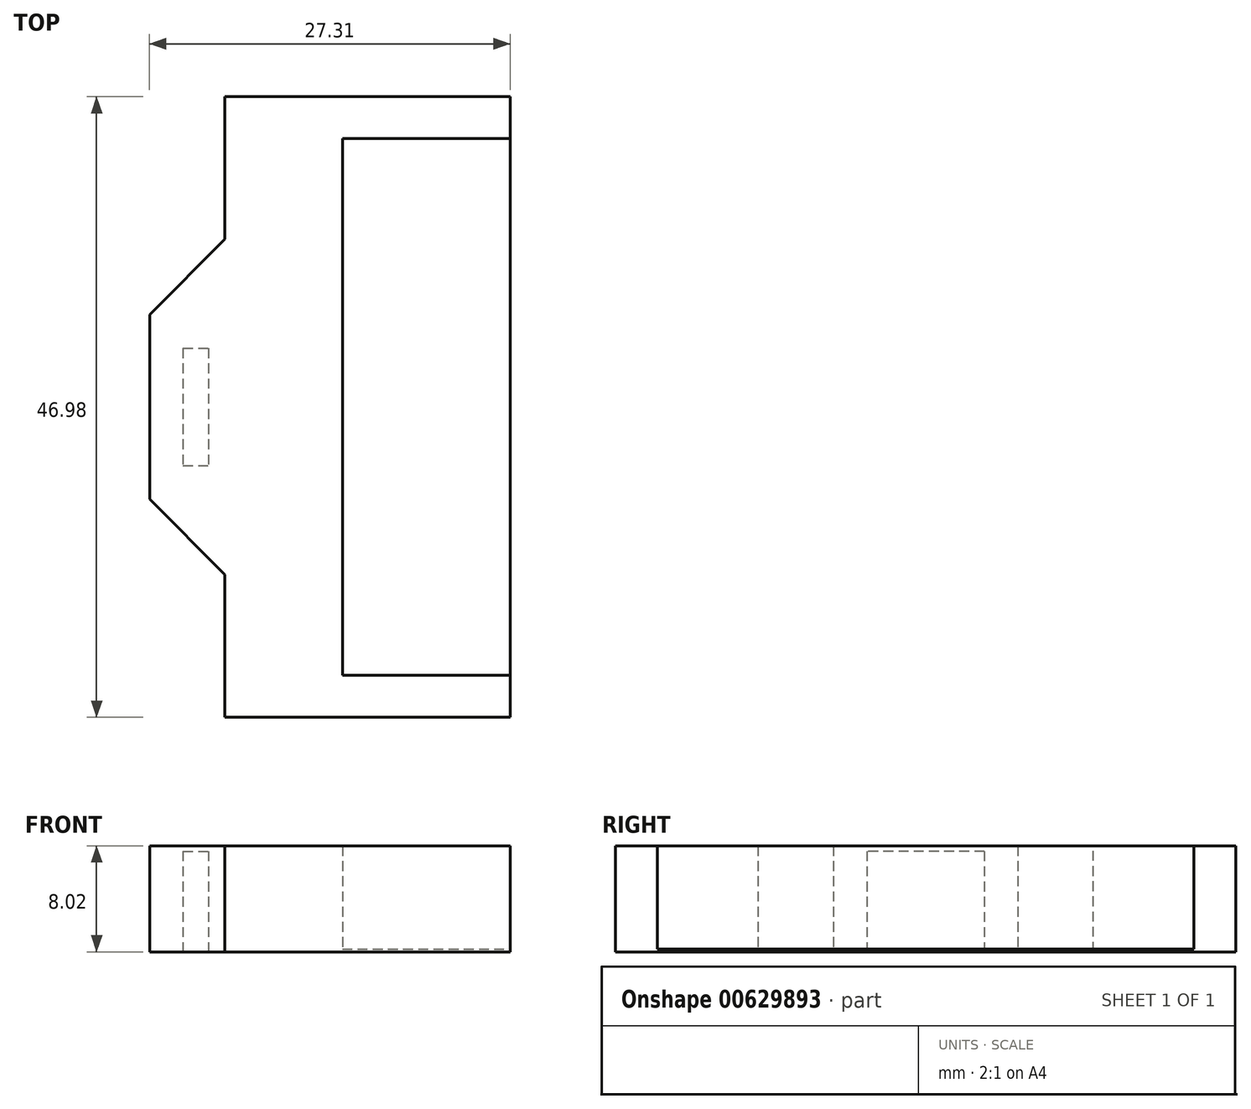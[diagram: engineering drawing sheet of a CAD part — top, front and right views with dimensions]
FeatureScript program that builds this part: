
annotation { "Feature Type Name" : "Feature", "Feature Type Description" : "" }
export const myFeature = defineFeature(function(context is Context, id is Id, definition is map)
    precondition{}
    {
        {
            var Q0;
            Q0=qCreatedBy(makeId("Top.planeOp"),FACE);
            var sketch = newSketch(context, id + "F0", { "sketchPlane" : qUnion([Q0])});
            skLineSegment(sketch, "E0", {"start": v(-14.6, 0) * mm, "end": v(-14.6, 6.99) * mm});
            skLineSegment(sketch, "E1", {"start": v(-14.6, 6.99) * mm, "end": v(-8.89, 6.99) * mm});
            skLineSegment(sketch, "E2", {"start": v(-8.89, 6.99) * mm, "end": v(-8.89, 23.5) * mm});
            skLineSegment(sketch, "E3", {"start": v(-8.89, 23.5) * mm, "end": v(12.7, 23.5) * mm});
            skLineSegment(sketch, "E4", {"start": v(12.7, 23.5) * mm, "end": v(12.7, 20.32) * mm});
            skLineSegment(sketch, "E5", {"start": v(12.7, 20.32) * mm, "end": v(0, 20.32) * mm});
            skLineSegment(sketch, "E6", {"start": v(0, 20.32) * mm, "end": v(0, 0) * mm});
            skLineSegment(sketch, "E7", {"start": v(0, 0) * mm, "end": v(0, -20.32) * mm});
            skLineSegment(sketch, "E8", {"start": v(0, -20.32) * mm, "end": v(12.7, -20.32) * mm});
            skLineSegment(sketch, "E9", {"start": v(12.7, -20.32) * mm, "end": v(12.7, -23.5) * mm});
            skLineSegment(sketch, "E10", {"start": v(12.7, -23.5) * mm, "end": v(-8.89, -23.5) * mm});
            skLineSegment(sketch, "E11", {"start": v(-8.89, -23.5) * mm, "end": v(-8.89, -6.99) * mm});
            skLineSegment(sketch, "E12", {"start": v(-8.9, -6.99) * mm, "end": v(-14.6, -6.99) * mm});
            skLineSegment(sketch, "E13", {"start": v(-14.6, -6.99) * mm, "end": v(-14.6, 0) * mm});
            skLineSegment(sketch, "E14.bottom", {"start": v(-12.07, 4.45) * mm, "end": v(-10.16, 4.45) * mm});
            skLineSegment(sketch, "E14.top", {"start": v(-12.07, -4.44) * mm, "end": v(-10.16, -4.44) * mm});
            skLineSegment(sketch, "E14.left", {"start": v(-12.07, 4.45) * mm, "end": v(-12.07, -4.44) * mm});
            skLineSegment(sketch, "E14.right", {"start": v(-10.16, 4.45) * mm, "end": v(-10.16, -4.44) * mm});
            skSolve(sketch);
        }
        {
            var Q0;
            Q0 = qSketchRegion(id + "F0", true);
            extrude(context, id + "F1", {"entities" : qUnion([Q0]), "depth" : 7.62 * mm, "offsetDistance" : 25.4 * mm});
        }
        {
            var Q0;
            Q0=makeQuery(id+"F1.opExtrude","CAP_FACE",FACE,{"disambiguationData":[OSD([sQuery(id+"F0.wireOp",EDGE,"E0"),sQuery(id+"F0.wireOp",EDGE,"E1"),sQuery(id+"F0.wireOp",EDGE,"E2"),sQuery(id+"F0.wireOp",EDGE,"E3"),sQuery(id+"F0.wireOp",EDGE,"E4"),sQuery(id+"F0.wireOp",EDGE,"E5"),sQuery(id+"F0.wireOp",EDGE,"E6"),sQuery(id+"F0.wireOp",EDGE,"E7"),sQuery(id+"F0.wireOp",EDGE,"E8"),sQuery(id+"F0.wireOp",EDGE,"E9"),sQuery(id+"F0.wireOp",EDGE,"E10"),sQuery(id+"F0.wireOp",EDGE,"E11"),sQuery(id+"F0.wireOp",EDGE,"E12"),sQuery(id+"F0.wireOp",EDGE,"E13"),sQuery(id+"F0.wireOp",EDGE,"E14.bottom"),sQuery(id+"F0.wireOp",EDGE,"E14.top"),sQuery(id+"F0.wireOp",EDGE,"E14.left"),sQuery(id+"F0.wireOp",EDGE,"E14.right")])],"isStart":false});
            var sketch = newSketch(context, id + "F2", { "sketchPlane" : qUnion([Q0])});
            skLineSegment(sketch, "E15.0", {"start": v(0, 20.32) * mm, "end": v(0, -20.32) * mm});
            skLineSegment(sketch, "E15.1", {"start": v(0, -20.32) * mm, "end": v(12.7, -20.32) * mm});
            skLineSegment(sketch, "E15.2", {"start": v(12.7, -20.32) * mm, "end": v(12.7, -23.5) * mm});
            skLineSegment(sketch, "E15.3", {"start": v(12.7, -23.5) * mm, "end": v(-8.89, -23.5) * mm});
            skLineSegment(sketch, "E15.4", {"start": v(-8.89, -23.5) * mm, "end": v(-8.89, -6.99) * mm});
            skLineSegment(sketch, "E15.5", {"start": v(-8.89, -6.99) * mm, "end": v(-14.6, -6.99) * mm});
            skLineSegment(sketch, "E15.6", {"start": v(-14.6, -6.99) * mm, "end": v(-14.6, 6.99) * mm});
            skLineSegment(sketch, "E15.7", {"start": v(-14.6, 6.99) * mm, "end": v(-8.89, 6.99) * mm});
            skLineSegment(sketch, "E15.8", {"start": v(-8.89, 6.99) * mm, "end": v(-8.89, 23.5) * mm});
            skLineSegment(sketch, "E15.9", {"start": v(-8.89, 23.5) * mm, "end": v(12.7, 23.5) * mm});
            skLineSegment(sketch, "E15.10", {"start": v(12.7, 20.32) * mm, "end": v(0, 20.32) * mm});
            skLineSegment(sketch, "E15.11", {"start": v(12.7, 23.5) * mm, "end": v(12.7, 20.32) * mm});
            skSolve(sketch);
        }
        {
            var Q0;
            Q0 = qSketchRegion(id + "F2", true);
            extrude(context, id + "F3", {"entities" : qUnion([Q0]), "operationType" : NewBodyOperationType.ADD, "depth" : .4 * mm, "offsetDistance" : 25.4 * mm});
        }
        {
            var Q0;
            Q0=makeQuery(id+"F1.opExtrude","CAP_FACE",FACE,{"disambiguationData":[OSD([sQuery(id+"F0.wireOp",EDGE,"E0"),sQuery(id+"F0.wireOp",EDGE,"E1"),sQuery(id+"F0.wireOp",EDGE,"E2"),sQuery(id+"F0.wireOp",EDGE,"E3"),sQuery(id+"F0.wireOp",EDGE,"E4"),sQuery(id+"F0.wireOp",EDGE,"E5"),sQuery(id+"F0.wireOp",EDGE,"E6"),sQuery(id+"F0.wireOp",EDGE,"E7"),sQuery(id+"F0.wireOp",EDGE,"E8"),sQuery(id+"F0.wireOp",EDGE,"E9"),sQuery(id+"F0.wireOp",EDGE,"E10"),sQuery(id+"F0.wireOp",EDGE,"E11"),sQuery(id+"F0.wireOp",EDGE,"E12"),sQuery(id+"F0.wireOp",EDGE,"E13"),sQuery(id+"F0.wireOp",EDGE,"E14.bottom"),sQuery(id+"F0.wireOp",EDGE,"E14.top"),sQuery(id+"F0.wireOp",EDGE,"E14.left"),sQuery(id+"F0.wireOp",EDGE,"E14.right")])],"isStart":true});
            var sketch = newSketch(context, id + "F4", { "sketchPlane" : qUnion([Q0])});
            skLineSegment(sketch, "E16.bottom", {"start": v(0, 20.32) * mm, "end": v(12.7, 20.32) * mm});
            skLineSegment(sketch, "E16.top", {"start": v(0, -20.32) * mm, "end": v(12.7, -20.32) * mm});
            skLineSegment(sketch, "E16.left", {"start": v(0, 20.32) * mm, "end": v(0, -20.32) * mm});
            skLineSegment(sketch, "E16.right", {"start": v(12.7, 20.32) * mm, "end": v(12.7, -20.32) * mm});
            skSolve(sketch);
        }
        {
            var Q0;
            Q0 = qSketchRegion(id + "F4", true);
            extrude(context, id + "F5", {"entities" : qUnion([Q0]), "operationType" : NewBodyOperationType.ADD, "oppositeDirection" : true, "depth" : .2 * mm, "offsetDistance" : 25.4 * mm});
        }
        {
            var Q0;
            Q0=makeQuery(id+"F3.boolean.opBoolean","MERGE",EDGE,{"derivedFrom":[makeQuery(id+"F1.opExtrude","SWEPT_EDGE",EDGE,{"disambiguationData":[OSD([sQuery(id+"F0.wireOp",EDGE,"E1"),sQuery(id+"F0.wireOp",EDGE,"E2")])]}),makeQuery(id+"F3.opExtrude","SWEPT_EDGE",EDGE,{"disambiguationData":[OSD([sQuery(id+"F2.wireOp",EDGE,"E15.7"),sQuery(id+"F2.wireOp",EDGE,"E15.8")])]})]});
            var Q1;
            Q1=makeQuery(id+"F3.boolean.opBoolean","MERGE",EDGE,{"derivedFrom":[makeQuery(id+"F1.opExtrude","SWEPT_EDGE",EDGE,{"disambiguationData":[OSD([sQuery(id+"F0.wireOp",EDGE,"E11"),sQuery(id+"F0.wireOp",EDGE,"E12")])]}),makeQuery(id+"F3.opExtrude","SWEPT_EDGE",EDGE,{"disambiguationData":[OSD([sQuery(id+"F2.wireOp",EDGE,"E15.4"),sQuery(id+"F2.wireOp",EDGE,"E15.5")])]})]});
            chamfer(context, id + "F6", {"entities" : qUnion([Q0, Q1]), "width" : 5.7 * mm, "tangentPropagation" : true});
        }
    });
